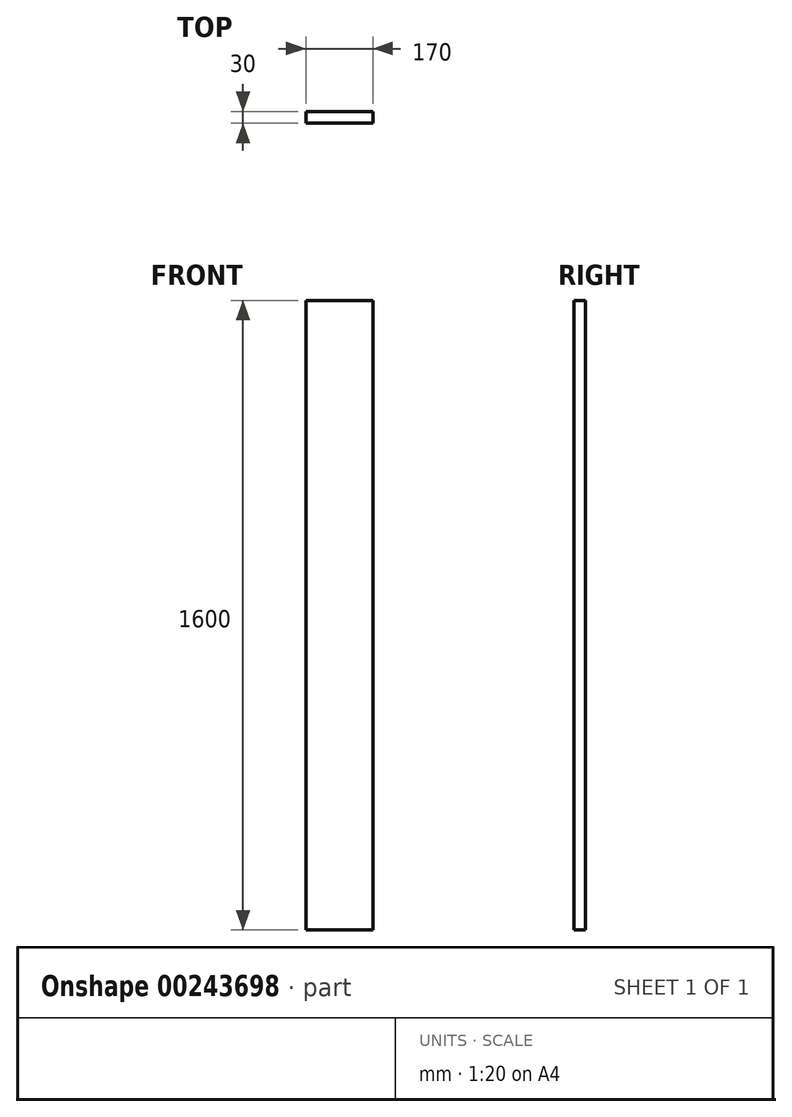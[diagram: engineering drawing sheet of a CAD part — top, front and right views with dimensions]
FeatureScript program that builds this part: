
annotation { "Feature Type Name" : "Feature", "Feature Type Description" : "" }
export const myFeature = defineFeature(function(context is Context, id is Id, definition is map)
    precondition{}
    {
        {
            var Q0;
            Q0=qCreatedBy(makeId("Front.planeOp"),FACE);
            var sketch = newSketch(context, id + "F0", { "sketchPlane" : qUnion([Q0])});
            skLineSegment(sketch, "E0.bottom", {"start": v(-85, 800) * mm, "end": v(85, 800) * mm});
            skLineSegment(sketch, "E0.top", {"start": v(-85, -800) * mm, "end": v(85, -800) * mm});
            skLineSegment(sketch, "E0.left", {"start": v(-85, 800) * mm, "end": v(-85, -800) * mm});
            skLineSegment(sketch, "E0.right", {"start": v(85, 800) * mm, "end": v(85, -800) * mm});
            skLineSegment(sketch, "E1", {"start": v(0, 800) * mm, "end": v(0, -800) * mm, "construction": true});
            skLineSegment(sketch, "E2", {"start": v(-85, 0) * mm, "end": v(85, 0) * mm, "construction": true});
            skSolve(sketch);
        }
        {
            var Q0;
            Q0=makeQuery(id+"F0.imprint","IMPRINT",FACE,{"disambiguationData":[TD([[makeQuery(id+"F0.imprint","IMPRINT",EDGE,{"derivedFrom":sQuery(id+"F0.wireOp",EDGE,"E0.bottom")}),-1.0]])]});
            extrude(context, id + "F1", {"entities" : qUnion([Q0]), "endBound" : BoundingType.SYMMETRIC, "depth" : 30 * mm});
        }
    });
